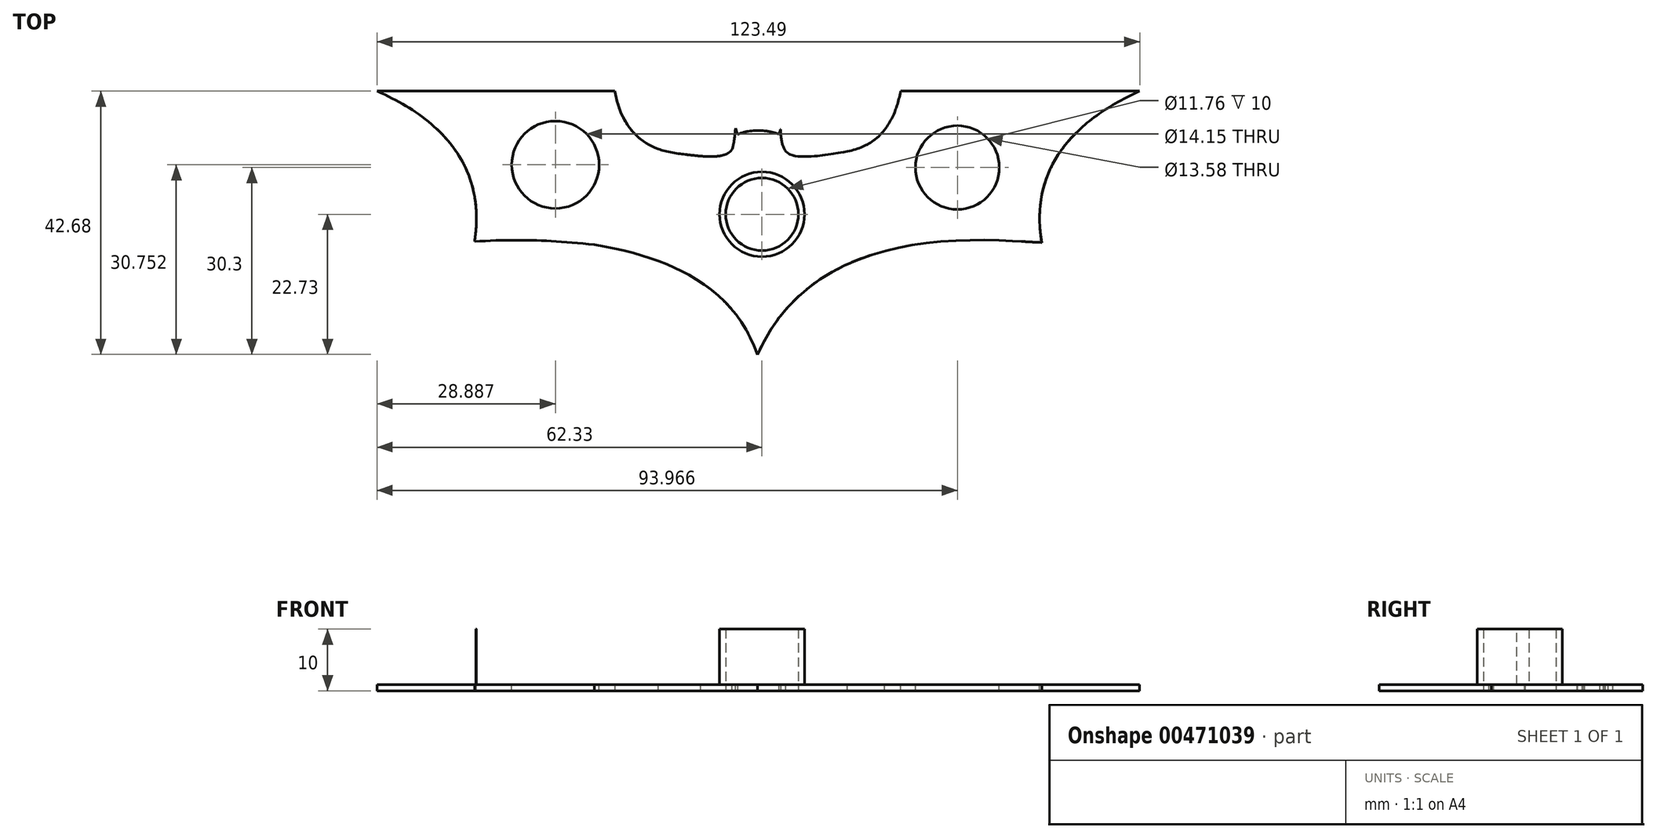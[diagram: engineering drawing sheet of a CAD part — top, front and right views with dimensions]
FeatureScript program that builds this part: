
annotation { "Feature Type Name" : "Feature", "Feature Type Description" : "" }
export const myFeature = defineFeature(function(context is Context, id is Id, definition is map)
    precondition{}
    {
        {
            var Q0;
            Q0=qCreatedBy(makeId("Top.planeOp"),FACE);
            var sketch = newSketch(context, id + "F0", { "sketchPlane" : qUnion([Q0])});
            skLineSegment(sketch, "E0", {"start": v(-67.27, 20.95) * mm, "end": v(-22.94, 20.95) * mm});
            skLineSegment(sketch, "E1", {"start": v(21.61, 20.95) * mm, "end": v(66.12, 20.95) * mm});
            skFitSpline(sketch, "E2", {"points": [v(-3.34, 14.22) * mm, v(2.08, 14.22) * mm], "startDerivative": vector(2.13, 0.75) * mm, "endDerivative": vector(6.84, -1.9) * mm});
            skFitSpline(sketch, "E3", {"points": [v(-22.94, 20.95) * mm, v(-16.46, 11.5) * mm], "startDerivative": vector(1.15, -9.76) * mm, "endDerivative": vector(14.26, -5.37) * mm});
            skFitSpline(sketch, "E4", {"points": [v(-16.46, 11.5) * mm, v(-9.84, 10.4) * mm], "startDerivative": vector(6.44, -2.07) * mm, "endDerivative": vector(6.31, -0.75) * mm});
            skFitSpline(sketch, "E5", {"points": [v(-4.68, 19.26) * mm, v(-3.34, 14.22) * mm], "startDerivative": vector(1.2, -5.44) * mm, "endDerivative": vector(2.2, -6.36) * mm});
            skFitSpline(sketch, "E6", {"points": [v(4.6, 10.85) * mm, v(13.64, 11.15) * mm], "startDerivative": vector(3.1, -3.3) * mm, "endDerivative": vector(7.86, 1.36) * mm});
            skFitSpline(sketch, "E7", {"points": [v(13.64, 11.15) * mm, v(19.08, 14.3) * mm], "startDerivative": vector(9.85, 2.22) * mm, "endDerivative": vector(3.21, 3.63) * mm});
            skFitSpline(sketch, "E8", {"points": [v(19.08, 14.3) * mm, v(21.61, 20.95) * mm], "startDerivative": vector(5.02, 6.83) * mm, "endDerivative": vector(1.23, 6.73) * mm});
            skFitSpline(sketch, "E9", {"points": [v(66.12, 20.95) * mm, v(46.52, -5.56) * mm], "startDerivative": vector(-12.53, -5.53) * mm, "endDerivative": vector(12.37, -55.76) * mm});
            skFitSpline(sketch, "E10", {"points": [v(46.52, -5.56) * mm, v(0, -23.6) * mm], "startDerivative": vector(-15.06, -1.3) * mm, "endDerivative": vector(-29.72, -70.8) * mm});
            skFitSpline(sketch, "E11", {"points": [v(0, -23.6) * mm, v(-0.67, -25.68) * mm], "startDerivative": vector(-0.9, -2.58) * mm, "endDerivative": vector(-0.4, -1.85) * mm});
            skFitSpline(sketch, "E12", {"points": [v(-27.28, -5.93) * mm, v(-47.75, -5.5) * mm], "startDerivative": vector(-19.8, 2.14) * mm, "endDerivative": vector(-23.86, -1.78) * mm});
            skFitSpline(sketch, "E13", {"points": [v(-67.27, 20.95) * mm, v(-47.75, -5.5) * mm], "startDerivative": vector(10.22, -5.14) * mm, "endDerivative": vector(-11.93, -57.86) * mm});
            skFitSpline(sketch, "E14", {"points": [v(-27.28, -5.93) * mm, v(-0.67, -25.68) * mm], "startDerivative": vector(71.13, -11.6) * mm, "endDerivative": vector(5, -10.16) * mm});
            skFitSpline(sketch, "E15", {"points": [v(2.08, 14.22) * mm, v(3.34, 19.3) * mm], "startDerivative": vector(1.29, 4.72) * mm, "endDerivative": vector(0.94, 5.64) * mm});
            skFitSpline(sketch, "E16", {"points": [v(-9.84, 10.4) * mm, v(-5.73, 10.99) * mm], "startDerivative": vector(3.94, -0.13) * mm, "endDerivative": vector(2.14, 2.4) * mm});
            skFitSpline(sketch, "E17", {"points": [v(-5.73, 10.99) * mm, v(-4.68, 19.26) * mm], "startDerivative": vector(2.08, 7.4) * mm, "endDerivative": vector(2.01, 5.33) * mm});
            skFitSpline(sketch, "E18", {"points": [v(4.6, 10.85) * mm, v(3.34, 19.3) * mm], "startDerivative": vector(-3.09, 4.58) * mm, "endDerivative": vector(-3.05, 9.7) * mm});
            skCircle(sketch, "E19", {"center": v(-33.44, 8.02) * mm, "radius": 6.08 * mm});
            skCircle(sketch, "E20", {"center": v(31.64, 7.57) * mm, "radius": 5.79 * mm});
            skCircle(sketch, "E21", {"center": v(0, 0) * mm, "radius": 5.88 * mm});
            skSolve(sketch);
        }
        {
            var Q0;
            Q0 = qSketchRegion(id + "F0", true);
            extrude(context, id + "F1", {"entities" : qUnion([Q0]), "depth" : 10 * mm});
        }
        {
            var Q0;
            Q0=makeQuery(id+"F1.opExtrude","CAP_FACE",FACE,{"disambiguationData":[OSD([sQuery(id+"F0.wireOp",EDGE,"E0"),sQuery(id+"F0.wireOp",EDGE,"E1"),sQuery(id+"F0.wireOp",EDGE,"E2"),sQuery(id+"F0.wireOp",EDGE,"E3"),sQuery(id+"F0.wireOp",EDGE,"E4"),sQuery(id+"F0.wireOp",EDGE,"E5"),sQuery(id+"F0.wireOp",EDGE,"E6"),sQuery(id+"F0.wireOp",EDGE,"E7"),sQuery(id+"F0.wireOp",EDGE,"E8"),sQuery(id+"F0.wireOp",EDGE,"E9"),sQuery(id+"F0.wireOp",EDGE,"E10"),sQuery(id+"F0.wireOp",EDGE,"E11"),sQuery(id+"F0.wireOp",EDGE,"E12"),sQuery(id+"F0.wireOp",EDGE,"E13"),sQuery(id+"F0.wireOp",EDGE,"E14"),sQuery(id+"F0.wireOp",EDGE,"E15"),sQuery(id+"F0.wireOp",EDGE,"E16"),sQuery(id+"F0.wireOp",EDGE,"E17"),sQuery(id+"F0.wireOp",EDGE,"E18")])],"isStart":false});
            shell(context, id + "F2", {"entities" : qUnion([Q0]), "thickness" : 1 * mm});
        }
        {
            var Q0;
            {var subQ0=sQuery(id+"F0.wireOp",EDGE,"E19");var subQ1=sQuery(id+"F0.wireOp",EDGE,"E18");var subQ2=sQuery(id+"F0.wireOp",EDGE,"E17");var subQ3=sQuery(id+"F0.wireOp",EDGE,"E16");var subQ4=sQuery(id+"F0.wireOp",EDGE,"E15");var subQ5=sQuery(id+"F0.wireOp",EDGE,"E14");var subQ6=sQuery(id+"F0.wireOp",EDGE,"E13");var subQ7=sQuery(id+"F0.wireOp",EDGE,"E12");var subQ8=sQuery(id+"F0.wireOp",EDGE,"E11");var subQ9=sQuery(id+"F0.wireOp",EDGE,"E10");var subQ10=sQuery(id+"F0.wireOp",EDGE,"E9");var subQ11=sQuery(id+"F0.wireOp",EDGE,"E8");var subQ12=sQuery(id+"F0.wireOp",EDGE,"E7");var subQ13=sQuery(id+"F0.wireOp",EDGE,"E6");var subQ14=sQuery(id+"F0.wireOp",EDGE,"E5");var subQ15=sQuery(id+"F0.wireOp",EDGE,"E4");var subQ16=sQuery(id+"F0.wireOp",EDGE,"E3");var subQ17=sQuery(id+"F0.wireOp",EDGE,"E2");var subQ18=sQuery(id+"F0.wireOp",EDGE,"E1");var subQ19=sQuery(id+"F0.wireOp",EDGE,"E0");Q0=makeQuery(id+"F2.opShell","OFFSET_FACE",FACE,{"disambiguationData":[OSD([subQ19,subQ18,subQ17,subQ16,subQ15,subQ14,subQ13,subQ12,subQ11,subQ10,subQ9,subQ8,subQ7,subQ6,subQ5,subQ4,subQ3,subQ2,subQ1,subQ0]),TDD([makeQuery(id+"F1.opExtrude","CAP_FACE",FACE,{"disambiguationData":[OSD([subQ19,subQ18,subQ17,subQ16,subQ15,subQ14,subQ13,subQ12,subQ11,subQ10,subQ9,subQ8,subQ7,subQ6,subQ5,subQ4,subQ3,subQ2,subQ1,subQ0])],"isStart":false})])]});}
            var Q1;
            Q1=sQuery(id+"F0.wireOp",EDGE,"E19");
            extrude(context, id + "F3", {"entities" : qUnion([Q0]), "operationType" : NewBodyOperationType.REMOVE, "surfaceEntities" : qUnion([Q1]), "oppositeDirection" : true, "depth" : 25 * mm});
        }
    });
